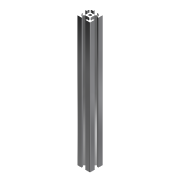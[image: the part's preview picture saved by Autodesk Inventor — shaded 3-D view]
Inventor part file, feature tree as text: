
AUTODESK INVENTOR PART (.ipt)
format: ipt  version: 2018 (Build 220112000, 112)  size: 167,424 bytes
history: native  units: mm
features: extrude x1, sketch x1
ambient origin geometry x8: Origin, YZ Plane, XZ Plane, XY Plane, X Axis, Y Axis, Z Axis, Center Point
bodies: Solid1 (feature_tree)
feature tree (2):
  extrude  "Extrusion1"  [1 undecoded]
  sketch  "Sketch1"  dims[d0=200.0mm d1=0.0mm]
note: 1 required parameter value undecoded (feature->parameter linkage not recoverable at this tier; creation-order binding heuristic only, values carry confidence <= 0.55)
